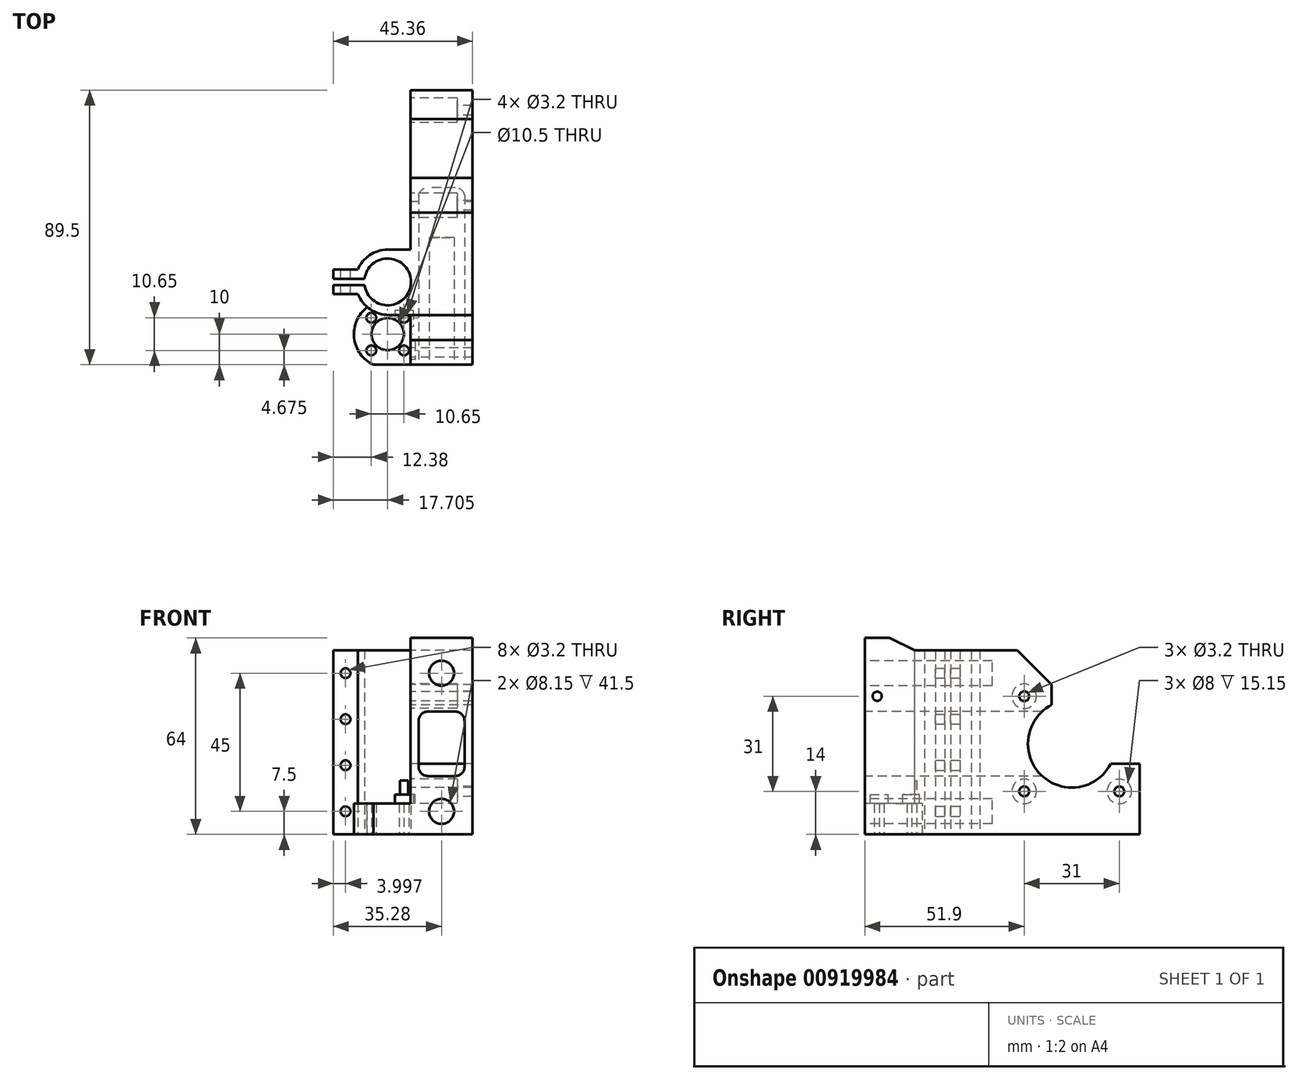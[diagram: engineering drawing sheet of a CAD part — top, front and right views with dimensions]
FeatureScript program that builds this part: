
annotation { "Feature Type Name" : "Feature", "Feature Type Description" : "" }
export const myFeature = defineFeature(function(context is Context, id is Id, definition is map)
    precondition{}
    {
        {
            var Q0;
            Q0=qCreatedBy(makeId("Top.planeOp"),FACE);
            var sketch = newSketch(context, id + "F0", { "sketchPlane" : qUnion([Q0])});
            skLineSegment(sketch, "E0.bottom", {"start": v(10.08, -44.75) * mm, "end": v(-10.07, -44.75) * mm});
            skLineSegment(sketch, "E0.top", {"start": v(10.08, 44.75) * mm, "end": v(-10.07, 44.75) * mm});
            skLineSegment(sketch, "E0.left", {"start": v(10.08, -44.75) * mm, "end": v(10.08, 44.75) * mm});
            skPoint(sketch, "E0.middle", {"position": v(0, 0) * mm});
            skCircle(sketch, "E1", {"center": v(-17.57, -34.75) * mm, "radius": 5 * mm});
            skArc(sketch, "E2", {"start": v(-17.46, -23.75) * mm, "mid": v(-17.58, -23.75) * mm, "end": v(-17.69, -23.75) * mm});
            skLineSegment(sketch, "E3", {"start": v(-17.69, -23.75) * mm, "end": v(-17.46, -23.75) * mm});
            skLineSegment(sketch, "E4", {"start": v(-10.07, -44.75) * mm, "end": v(-22.16, -44.75) * mm});
            skLineSegment(sketch, "E5.trimOffspring", {"start": v(-10.07, -7.25) * mm, "end": v(-10.07, 44.75) * mm});
            skCircle(sketch, "E6", {"center": v(-12.25, -40.08) * mm, "radius": 1.6 * mm});
            skCircle(sketch, "E7", {"center": v(-12.25, -29.43) * mm, "radius": 1.6 * mm});
            skCircle(sketch, "E8", {"center": v(-22.9, -29.43) * mm, "radius": 1.6 * mm});
            skCircle(sketch, "E9", {"center": v(-22.9, -40.08) * mm, "radius": 1.6 * mm});
            skPoint(sketch, "E10", {"position": v(-17.57, -17.75) * mm});
            skArc(sketch, "E11", {"start": v(-25, -18.75) * mm, "mid": v(-10.07, -17.75) * mm, "end": v(-25, -16.75) * mm});
            skArc(sketch, "E12", {"start": v(-17.5, -7.25) * mm, "mid": v(-23.38, -9) * mm, "end": v(-27.28, -13.75) * mm});
            skLineSegment(sketch, "E13", {"start": v(-17.66, -7.25) * mm, "end": v(-10.07, -7.25) * mm});
            skArc(sketch, "E14.trimOffspring", {"start": v(-24.15, -25.93) * mm, "mid": v(-28.51, -35.91) * mm, "end": v(-22.16, -44.75) * mm});
            skLineSegment(sketch, "E15.bottom", {"start": v(-27.28, -13.75) * mm, "end": v(-34.18, -13.75) * mm});
            skLineSegment(sketch, "E15.top", {"start": v(-27.28, -21.75) * mm, "end": v(-34.18, -21.75) * mm});
            skLineSegment(sketch, "E15.right", {"start": v(-34.18, -13.75) * mm, "end": v(-34.18, -16.75) * mm});
            skPoint(sketch, "E15.middle", {"position": v(-26.68, -17.75) * mm});
            skLineSegment(sketch, "E16.bottom", {"start": v(-25, -16.75) * mm, "end": v(-34.18, -16.75) * mm});
            skLineSegment(sketch, "E16.top", {"start": v(-25, -18.75) * mm, "end": v(-34.18, -18.75) * mm});
            skLineSegment(sketch, "E17.trimOffspring", {"start": v(-34.18, -18.75) * mm, "end": v(-34.18, -21.75) * mm});
            skArc(sketch, "E18.trimOffspring", {"start": v(-27.28, -21.75) * mm, "mid": v(-25.98, -24.04) * mm, "end": v(-24.15, -25.93) * mm});
            skLineSegment(sketch, "E19", {"start": v(-10.07, -44.75) * mm, "end": v(-10.07, -25.89) * mm});
            skLineSegment(sketch, "E20", {"start": v(-24.15, -25.93) * mm, "end": v(-10.07, -25.89) * mm});
            skSolve(sketch);
        }
        {
            var Q0;
            Q0=makeQuery(id+"F0.imprint","IMPRINT",FACE,{"disambiguationData":[TD([[makeQuery(id+"F0.imprint","IMPRINT",EDGE,{"derivedFrom":sQuery(id+"F0.wireOp",EDGE,"E1")}),-1.0]])]});
            var Q1;
            Q1=makeQuery(id+"F0.imprint","IMPRINT",FACE,{"disambiguationData":[TD([[makeQuery(id+"F0.imprint","IMPRINT",EDGE,{"derivedFrom":sQuery(id+"F0.wireOp",EDGE,"E0.bottom")}),-1.0]])]});
            extrude(context, id + "F1", {"entities" : qUnion([Q0, Q1]), "depth" : 10 * mm, "offsetDistance" : 25 * mm});
        }
        {
            var Q0;
            Q0=makeQuery(id+"F1.opExtrude","CAP_FACE",FACE,{"disambiguationData":[OSD([sQuery(id+"F0.wireOp",EDGE,"E0.bottom"),sQuery(id+"F0.wireOp",EDGE,"E0.top"),sQuery(id+"F0.wireOp",EDGE,"E0.left"),sQuery(id+"F0.wireOp",EDGE,"E1"),sQuery(id+"F0.wireOp",EDGE,"E4"),sQuery(id+"F0.wireOp",EDGE,"E5.trimOffspring"),sQuery(id+"F0.wireOp",EDGE,"E6"),sQuery(id+"F0.wireOp",EDGE,"E7"),sQuery(id+"F0.wireOp",EDGE,"E8"),sQuery(id+"F0.wireOp",EDGE,"E9"),sQuery(id+"F0.wireOp",EDGE,"E11"),sQuery(id+"F0.wireOp",EDGE,"E12"),sQuery(id+"F0.wireOp",EDGE,"E13"),sQuery(id+"F0.wireOp",EDGE,"E14.trimOffspring"),sQuery(id+"F0.wireOp",EDGE,"E15.bottom"),sQuery(id+"F0.wireOp",EDGE,"E15.top"),sQuery(id+"F0.wireOp",EDGE,"E15.right"),sQuery(id+"F0.wireOp",EDGE,"E16.bottom"),sQuery(id+"F0.wireOp",EDGE,"E16.top"),sQuery(id+"F0.wireOp",EDGE,"E17.trimOffspring"),sQuery(id+"F0.wireOp",EDGE,"E18.trimOffspring")])],"isStart":false});
            var sketch = newSketch(context, id + "F2", { "sketchPlane" : qUnion([Q0])});
            skLineSegment(sketch, "E21", {"start": v(-24.15, -25.93) * mm, "end": v(-10.07, -25.93) * mm});
            skLineSegment(sketch, "E22", {"start": v(-10.07, -25.93) * mm, "end": v(-10.07, -44.75) * mm});
            skSolve(sketch);
        }
        {
            var Q0;
            Q0=makeQuery(id+"F2.imprint","IMPRINT",FACE,{"disambiguationData":[TD([[makeQuery(id+"F2.imprint","IMPRINT",EDGE,{"derivedFrom":sQuery(id+"F2.wireOp",EDGE,"E21")}),1.0]])]});
            extrude(context, id + "F3", {"entities" : qUnion([Q0]), "operationType" : NewBodyOperationType.ADD, "depth" : 50 * mm, "offsetDistance" : 25 * mm});
        }
        {
            var Q0;
            Q0=makeQuery(id+"F3.opExtrude","CAP_FACE",FACE,{"disambiguationData":[OSD([sQuery(id+"F0.wireOp",EDGE,"E0.bottom"),sQuery(id+"F0.wireOp",EDGE,"E0.top"),sQuery(id+"F0.wireOp",EDGE,"E0.left"),sQuery(id+"F0.wireOp",EDGE,"E4"),sQuery(id+"F0.wireOp",EDGE,"E5.trimOffspring"),sQuery(id+"F0.wireOp",EDGE,"E11"),sQuery(id+"F0.wireOp",EDGE,"E12"),sQuery(id+"F0.wireOp",EDGE,"E13"),sQuery(id+"F0.wireOp",EDGE,"E15.bottom"),sQuery(id+"F0.wireOp",EDGE,"E15.top"),sQuery(id+"F0.wireOp",EDGE,"E15.right"),sQuery(id+"F0.wireOp",EDGE,"E16.bottom"),sQuery(id+"F0.wireOp",EDGE,"E16.top"),sQuery(id+"F0.wireOp",EDGE,"E17.trimOffspring"),sQuery(id+"F0.wireOp",EDGE,"E18.trimOffspring"),sQuery(id+"F2.wireOp",EDGE,"E21"),sQuery(id+"F2.wireOp",EDGE,"E22")])],"isStart":false});
            var sketch = newSketch(context, id + "F4", { "sketchPlane" : qUnion([Q0])});
            skArc(sketch, "E23", {"start": v(-27.28, -21.75) * mm, "mid": v(-23.23, -26.7) * mm, "end": v(-17.11, -28.53) * mm});
            skPoint(sketch, "E24.startSnap0", {"position": v(-17.11, -25.93) * mm});
            skLineSegment(sketch, "E25", {"start": v(-17.11, -28.53) * mm, "end": v(-10.07, -28.53) * mm});
            skSolve(sketch);
        }
        {
            var Q0;
            Q0=makeQuery(id+"F4.imprint","IMPRINT",FACE,{"disambiguationData":[TD([[makeQuery(id+"F4.imprint","IMPRINT",EDGE,{"derivedFrom":sQuery(id+"F4.wireOp",EDGE,"E23")}),1.0]])]});
            extrude(context, id + "F5", {"entities" : qUnion([Q0]), "operationType" : NewBodyOperationType.ADD, "oppositeDirection" : true, "depth" : 50 * mm, "offsetDistance" : 25 * mm});
        }
        {
            var Q0;
            Q0=makeQuery(id+"F5.opExtrude","SWEPT_FACE",FACE,{"disambiguationData":[OSD([sQuery(id+"F4.wireOp",EDGE,"E25")])]});
            var sketch = newSketch(context, id + "F6", { "sketchPlane" : qUnion([Q0])});
            skLineSegment(sketch, "E26.bottom", {"start": v(-9.25, 10) * mm, "end": v(-15.25, 10) * mm});
            skLineSegment(sketch, "E26.top", {"start": v(-9.25, 13) * mm, "end": v(-15.25, 13) * mm});
            skLineSegment(sketch, "E26.left", {"start": v(-9.25, 10) * mm, "end": v(-9.25, 13) * mm});
            skLineSegment(sketch, "E26.right", {"start": v(-15.25, 10) * mm, "end": v(-15.25, 13) * mm});
            skPoint(sketch, "E26.middle", {"position": v(-12.25, 11.5) * mm});
            skSolve(sketch);
        }
        {
            var Q0;
            Q0 = qSketchRegion(id + "F6", true);
            extrude(context, id + "F7", {"entities" : qUnion([Q0]), "operationType" : NewBodyOperationType.REMOVE, "oppositeDirection" : true, "depth" : 1.5 * mm, "offsetDistance" : 25 * mm});
        }
        {
            var Q0;
            Q0=makeQuery(id+"F7.boolean.opBoolean","MERGE",FACE,{"derivedFrom":[makeQuery(id+"F1.opExtrude","CAP_FACE",FACE,{"disambiguationData":[OSD([sQuery(id+"F0.wireOp",EDGE,"E0.bottom"),sQuery(id+"F0.wireOp",EDGE,"E0.top"),sQuery(id+"F0.wireOp",EDGE,"E0.left"),sQuery(id+"F0.wireOp",EDGE,"E1"),sQuery(id+"F0.wireOp",EDGE,"E4"),sQuery(id+"F0.wireOp",EDGE,"E5.trimOffspring"),sQuery(id+"F0.wireOp",EDGE,"E6"),sQuery(id+"F0.wireOp",EDGE,"E7"),sQuery(id+"F0.wireOp",EDGE,"E8"),sQuery(id+"F0.wireOp",EDGE,"E9"),sQuery(id+"F0.wireOp",EDGE,"E11"),sQuery(id+"F0.wireOp",EDGE,"E12"),sQuery(id+"F0.wireOp",EDGE,"E13"),sQuery(id+"F0.wireOp",EDGE,"E14.trimOffspring"),sQuery(id+"F0.wireOp",EDGE,"E15.bottom"),sQuery(id+"F0.wireOp",EDGE,"E15.top"),sQuery(id+"F0.wireOp",EDGE,"E15.right"),sQuery(id+"F0.wireOp",EDGE,"E16.bottom"),sQuery(id+"F0.wireOp",EDGE,"E16.top"),sQuery(id+"F0.wireOp",EDGE,"E17.trimOffspring"),sQuery(id+"F0.wireOp",EDGE,"E18.trimOffspring")])],"isStart":false})],"fromTools":[makeQuery(id+"F7.opExtrude","SWEPT_FACE",FACE,{"disambiguationData":[OSD([sQuery(id+"F6.wireOp",EDGE,"E26.bottom")])]})]});
            var sketch = newSketch(context, id + "F8", { "sketchPlane" : qUnion([Q0])});
            skCircle(sketch, "E27", {"center": v(-12.25, -29.43) * mm, "radius": 1.6 * mm});
            skCircle(sketch, "E28", {"center": v(-12.25, -40.08) * mm, "radius": 1.6 * mm});
            skSolve(sketch);
        }
        {
            var Q0;
            Q0=makeQuery(id+"F3.opExtrude","SWEPT_FACE",FACE,{"disambiguationData":[OSD([sQuery(id+"F2.wireOp",EDGE,"E22")])]});
            var sketch = newSketch(context, id + "F9", { "sketchPlane" : qUnion([Q0])});
            skLineSegment(sketch, "E29.bottom", {"start": v(32.43, 10) * mm, "end": v(26.43, 10) * mm});
            skLineSegment(sketch, "E29.top", {"start": v(32.43, 13) * mm, "end": v(26.43, 13) * mm});
            skLineSegment(sketch, "E29.left", {"start": v(32.43, 10) * mm, "end": v(32.43, 13) * mm});
            skLineSegment(sketch, "E29.right", {"start": v(26.43, 10) * mm, "end": v(26.43, 13) * mm});
            skPoint(sketch, "E29.middle", {"position": v(29.43, 11.5) * mm});
            skLineSegment(sketch, "E30.bottom", {"start": v(43.03, 10) * mm, "end": v(37.12, 10) * mm});
            skLineSegment(sketch, "E30.top", {"start": v(43.03, 13) * mm, "end": v(37.12, 13) * mm});
            skLineSegment(sketch, "E30.left", {"start": v(43.03, 10) * mm, "end": v(43.03, 13) * mm});
            skLineSegment(sketch, "E30.right", {"start": v(37.12, 10) * mm, "end": v(37.12, 13) * mm});
            skPoint(sketch, "E30.middle", {"position": v(40.08, 11.5) * mm});
            skSolve(sketch);
        }
        {
            var Q0;
            {var subQ6=sQuery(id+"F9.wireOp",EDGE,"E29.left");Q0=makeQuery(id+"F9.imprint","IMPRINT",FACE,{"disambiguationData":[TD([[makeQuery(id+"F9.imprint","IMPRINT",EDGE,{"derivedFrom":subQ6}),1.0]])]});}
            var Q1;
            Q1=makeQuery(id+"F9.imprint","IMPRINT",FACE,{"disambiguationData":[TD([[makeQuery(id+"F9.imprint","IMPRINT",EDGE,{"derivedFrom":sQuery(id+"F9.wireOp",EDGE,"E30.bottom")}),1.0]])]});
            extrude(context, id + "F10", {"entities" : qUnion([Q0, Q1]), "operationType" : NewBodyOperationType.REMOVE, "oppositeDirection" : true, "depth" : 1.5 * mm, "offsetDistance" : 25 * mm});
        }
        {
            var Q0;
            Q0=makeQuery(id+"F10.boolean.opBoolean","COPY",FACE,{"derivedFrom":makeQuery(id+"F10.opExtrude","SWEPT_FACE",FACE,{"disambiguationData":[OSD([sQuery(id+"F2.wireOp",EDGE,"E22"),sQuery(id+"F4.wireOp",EDGE,"E25")])]})});
            extrude(context, id + "F11", {"entities" : qUnion([Q0]), "operationType" : NewBodyOperationType.ADD, "depth" : 3.97 * mm, "offsetDistance" : 25 * mm});
        }
        {
            var Q0;
            {var subQ0=sQuery(id+"F0.wireOp",EDGE,"E15.bottom");Q0=makeQuery(id+"F3.boolean.opBoolean","MERGE",FACE,{"derivedFrom":[makeQuery(id+"F1.opExtrude","SWEPT_FACE",FACE,{"disambiguationData":[OSD([subQ0])]}),makeQuery(id+"F3.opExtrude","SWEPT_FACE",FACE,{"disambiguationData":[OSD([subQ0])]})]});}
            var sketch = newSketch(context, id + "F12", { "sketchPlane" : qUnion([Q0])});
            skCircle(sketch, "E31", {"center": v(31.28, 52.5) * mm, "radius": 1.6 * mm});
            skCircle(sketch, "E32", {"center": v(31.28, 37.5) * mm, "radius": 1.6 * mm});
            skCircle(sketch, "E33", {"center": v(31.28, 22.5) * mm, "radius": 1.6 * mm});
            skCircle(sketch, "E34", {"center": v(31.28, 7.5) * mm, "radius": 1.6 * mm});
            skSolve(sketch);
        }
        {
            var Q0;
            Q0=makeQuery(id+"F12.imprint","IMPRINT",FACE,{"disambiguationData":[TD([[makeQuery(id+"F12.imprint","IMPRINT",EDGE,{"derivedFrom":sQuery(id+"F12.wireOp",EDGE,"E31")}),1.0]])]});
            var Q1;
            Q1=makeQuery(id+"F12.imprint","IMPRINT",FACE,{"disambiguationData":[TD([[makeQuery(id+"F12.imprint","IMPRINT",EDGE,{"derivedFrom":sQuery(id+"F12.wireOp",EDGE,"E32")}),1.0]])]});
            var Q2;
            Q2=makeQuery(id+"F12.imprint","IMPRINT",FACE,{"disambiguationData":[TD([[makeQuery(id+"F12.imprint","IMPRINT",EDGE,{"derivedFrom":sQuery(id+"F12.wireOp",EDGE,"E33")}),1.0]])]});
            var Q3;
            Q3=makeQuery(id+"F12.imprint","IMPRINT",FACE,{"disambiguationData":[TD([[makeQuery(id+"F12.imprint","IMPRINT",EDGE,{"derivedFrom":sQuery(id+"F12.wireOp",EDGE,"E34")}),1.0]])]});
            extrude(context, id + "F13", {"entities" : qUnion([Q0, Q1, Q2, Q3]), "operationType" : NewBodyOperationType.REMOVE, "oppositeDirection" : true, "depth" : 25 * mm, "offsetDistance" : 25 * mm});
        }
        {
            var Q0;
            {var subQ0=sQuery(id+"F0.wireOp",EDGE,"E15.right");Q0=makeQuery(id+"F3.boolean.opBoolean","MERGE",FACE,{"derivedFrom":[makeQuery(id+"F1.opExtrude","SWEPT_FACE",FACE,{"disambiguationData":[OSD([subQ0])]}),makeQuery(id+"F3.opExtrude","SWEPT_FACE",FACE,{"disambiguationData":[OSD([subQ0])]})]});}
            var Q1;
            {var subQ0=sQuery(id+"F0.wireOp",EDGE,"E17.trimOffspring");Q1=makeQuery(id+"F3.boolean.opBoolean","MERGE",FACE,{"derivedFrom":[makeQuery(id+"F1.opExtrude","SWEPT_FACE",FACE,{"disambiguationData":[OSD([subQ0])]}),makeQuery(id+"F3.opExtrude","SWEPT_FACE",FACE,{"disambiguationData":[OSD([subQ0])]})]});}
            extrude(context, id + "F14", {"entities" : qUnion([Q0, Q1]), "operationType" : NewBodyOperationType.ADD, "depth" : 1.1 * mm, "offsetDistance" : 25 * mm});
        }
        {
            var Q0;
            {var subQ0=sQuery(id+"F0.wireOp",EDGE,"E14.trimOffspring");var subQ1=sQuery(id+"F0.wireOp",EDGE,"E18.trimOffspring");var subQ3=sQuery(id+"F4.wireOp",EDGE,"E23");Q0=makeQuery(id+"F5.boolean.opBoolean","SPLIT",FACE,{"disambiguationData":[TD([makeQuery(id+"F1.opExtrude","SWEPT_FACE",FACE,{"disambiguationData":[OSD([subQ0])]})])],"derivedFrom":makeQuery(id+"F5.opExtrude","CAP_FACE",FACE,{"disambiguationData":[OSD([subQ1,sQuery(id+"F2.wireOp",EDGE,"E21"),sQuery(id+"F2.wireOp",EDGE,"E22"),subQ3,sQuery(id+"F4.wireOp",EDGE,"E25")])],"isStart":false})});}
            extrude(context, id + "F15", {"entities" : qUnion([Q0]), "operationType" : NewBodyOperationType.ADD, "depth" : 10 * mm, "offsetDistance" : 25 * mm});
        }
        {
            var Q0;
            {var subQ0=sQuery(id+"F0.wireOp",EDGE,"E5.trimOffspring");Q0=makeQuery(id+"F3.boolean.opBoolean","MERGE",FACE,{"derivedFrom":[makeQuery(id+"F1.opExtrude","SWEPT_FACE",FACE,{"disambiguationData":[OSD([subQ0])]}),makeQuery(id+"F3.opExtrude","SWEPT_FACE",FACE,{"disambiguationData":[OSD([subQ0])]})]});}
            var sketch = newSketch(context, id + "F16", { "sketchPlane" : qUnion([Q0])});
            skCircle(sketch, "E35", {"center": v(-38.15, 14) * mm, "radius": 1.6 * mm});
            skCircle(sketch, "E36", {"center": v(-7.15, 45) * mm, "radius": 1.6 * mm});
            skCircle(sketch, "E37", {"center": v(-7.15, 14) * mm, "radius": 1.6 * mm});
            skCircle(sketch, "E38", {"center": v(-7.15, 45) * mm, "radius": 4 * mm});
            skCircle(sketch, "E39", {"center": v(-7.15, 14) * mm, "radius": 4 * mm});
            skCircle(sketch, "E40", {"center": v(-38.15, 14) * mm, "radius": 4 * mm});
            skSolve(sketch);
        }
        {
            var Q0;
            Q0=makeQuery(id+"F16.imprint","IMPRINT",FACE,{"disambiguationData":[TD([[makeQuery(id+"F16.imprint","IMPRINT",EDGE,{"derivedFrom":sQuery(id+"F16.wireOp",EDGE,"E36")}),1.0]])]});
            var Q1;
            Q1=makeQuery(id+"F16.imprint","IMPRINT",FACE,{"disambiguationData":[TD([[makeQuery(id+"F16.imprint","IMPRINT",EDGE,{"derivedFrom":sQuery(id+"F16.wireOp",EDGE,"E37")}),1.0]])]});
            var Q2;
            Q2=makeQuery(id+"F16.imprint","IMPRINT",FACE,{"disambiguationData":[TD([[makeQuery(id+"F16.imprint","IMPRINT",EDGE,{"derivedFrom":sQuery(id+"F16.wireOp",EDGE,"E35")}),1.0]])]});
            extrude(context, id + "F17", {"entities" : qUnion([Q0, Q1, Q2]), "operationType" : NewBodyOperationType.REMOVE, "endBound" : BoundingType.THROUGH_ALL, "oppositeDirection" : true, "depth" : 25 * mm, "offsetDistance" : 25 * mm});
        }
        {
            var Q0;
            Q0=makeQuery(id+"F16.imprint","IMPRINT",FACE,{"disambiguationData":[TD([[makeQuery(id+"F16.imprint","IMPRINT",EDGE,{"derivedFrom":sQuery(id+"F16.wireOp",EDGE,"E36")}),-1.0]])]});
            var Q1;
            Q1=makeQuery(id+"F16.imprint","IMPRINT",FACE,{"disambiguationData":[TD([[makeQuery(id+"F16.imprint","IMPRINT",EDGE,{"derivedFrom":sQuery(id+"F16.wireOp",EDGE,"E37")}),-1.0]])]});
            var Q2;
            Q2=makeQuery(id+"F16.imprint","IMPRINT",FACE,{"disambiguationData":[TD([[makeQuery(id+"F16.imprint","IMPRINT",EDGE,{"derivedFrom":sQuery(id+"F16.wireOp",EDGE,"E35")}),-1.0]])]});
            extrude(context, id + "F18", {"entities" : qUnion([Q0, Q1, Q2]), "operationType" : NewBodyOperationType.REMOVE, "oppositeDirection" : true, "depth" : 17.15 * mm, "offsetDistance" : 25 * mm});
        }
        {
            var Q0;
            {var subQ0=sQuery(id+"F0.wireOp",EDGE,"E5.trimOffspring");Q0=makeQuery(id+"F3.boolean.opBoolean","MERGE",FACE,{"derivedFrom":[makeQuery(id+"F1.opExtrude","SWEPT_FACE",FACE,{"disambiguationData":[OSD([subQ0])]}),makeQuery(id+"F3.opExtrude","SWEPT_FACE",FACE,{"disambiguationData":[OSD([subQ0])]})]});}
            var sketch = newSketch(context, id + "F19", { "sketchPlane" : qUnion([Q0])});
            skCircle(sketch, "E41", {"center": v(-22.65, 29.5) * mm, "radius": 14.25 * mm});
            skCircle(sketch, "E42", {"center": v(-7.15, 45) * mm, "radius": 0.81 * mm});
            skCircle(sketch, "E43", {"center": v(-7.15, 14) * mm, "radius": 1.4 * mm});
            skCircle(sketch, "E44", {"center": v(-38.15, 14) * mm, "radius": 0.92 * mm});
            skSolve(sketch);
        }
        {
            var Q0;
            Q0=makeQuery(id+"F19.imprint","IMPRINT",FACE,{"disambiguationData":[TD([[makeQuery(id+"F19.imprint","IMPRINT",EDGE,{"derivedFrom":sQuery(id+"F19.wireOp",EDGE,"E41")}),1.0]])]});
            extrude(context, id + "F20", {"entities" : qUnion([Q0]), "operationType" : NewBodyOperationType.REMOVE, "endBound" : BoundingType.THROUGH_ALL, "oppositeDirection" : true, "depth" : 25 * mm, "offsetDistance" : 25 * mm});
        }
        {
            var Q0;
            {var subQ0=sQuery(id+"F0.wireOp",EDGE,"E4");var subQ1=sQuery(id+"F0.wireOp",EDGE,"E0.bottom");Q0=makeQuery(id+"F3.boolean.opBoolean","MERGE",FACE,{"derivedFrom":[makeQuery(id+"F1.opExtrude","SWEPT_FACE",FACE,{"disambiguationData":[OSD([subQ1,subQ0])]}),makeQuery(id+"F3.opExtrude","SWEPT_FACE",FACE,{"disambiguationData":[OSD([subQ1,subQ0])]})]});}
            var sketch = newSketch(context, id + "F21", { "sketchPlane" : qUnion([Q0])});
            skLineSegment(sketch, "E45.bottom", {"start": v(7.48, 19) * mm, "end": v(-7.47, 19) * mm});
            skLineSegment(sketch, "E45.top", {"start": v(7.48, 40) * mm, "end": v(-7.47, 40) * mm});
            skLineSegment(sketch, "E45.left", {"start": v(7.48, 19) * mm, "end": v(7.47, 40) * mm});
            skLineSegment(sketch, "E45.right", {"start": v(-7.47, 19) * mm, "end": v(-7.47, 40) * mm});
            skPoint(sketch, "E45.middle", {"position": v(0, 29.5) * mm});
            skSolve(sketch);
        }
        {
            var Q0;
            Q0 = qSketchRegion(id + "F21", true);
            extrude(context, id + "F22", {"entities" : qUnion([Q0]), "operationType" : NewBodyOperationType.REMOVE, "oppositeDirection" : true, "depth" : 62.2 * mm, "offsetDistance" : 25 * mm});
        }
        {
            var Q0;
            {var subQ0=sQuery(id+"F0.wireOp",EDGE,"E5.trimOffspring");Q0=makeQuery(id+"F3.boolean.opBoolean","MERGE",FACE,{"derivedFrom":[makeQuery(id+"F1.opExtrude","SWEPT_FACE",FACE,{"disambiguationData":[OSD([subQ0])]}),makeQuery(id+"F3.opExtrude","SWEPT_FACE",FACE,{"disambiguationData":[OSD([subQ0])]})]});}
            var sketch = newSketch(context, id + "F23", { "sketchPlane" : qUnion([Q0])});
            skLineSegment(sketch, "E46", {"start": v(-35.33, 23) * mm, "end": v(-44.75, 23) * mm});
            skLineSegment(sketch, "E47", {"start": v(-16.15, 42.18) * mm, "end": v(-16.15, 48.73) * mm});
            skLineSegment(sketch, "E48", {"start": v(-16.15, 48.73) * mm, "end": v(-4.88, 60) * mm});
            skSolve(sketch);
        }
        {
            var Q0;
            Q0 = qSketchRegion(id + "F23", true);
            var Q1;
            {var subQ7=sQuery(id+"F23.wireOp",EDGE,"E46");Q1=makeQuery(id+"F23.imprint","IMPRINT",FACE,{"disambiguationData":[TD([[makeQuery(id+"F23.imprint","IMPRINT",EDGE,{"derivedFrom":subQ7}),-1.0]])]});}
            extrude(context, id + "F24", {"entities" : qUnion([Q0, Q1]), "operationType" : NewBodyOperationType.REMOVE, "endBound" : BoundingType.THROUGH_ALL, "oppositeDirection" : true, "depth" : 25 * mm, "offsetDistance" : 25 * mm});
        }
        {
            var Q0;
            Q0=makeQuery(id+"F3.opExtrude","SWEPT_FACE",FACE,{"disambiguationData":[OSD([sQuery(id+"F2.wireOp",EDGE,"E22")])]});
            var sketch = newSketch(context, id + "F25", { "sketchPlane" : qUnion([Q0])});
            skCircle(sketch, "E49", {"center": v(40.75, 56) * mm, "radius": 1.5 * mm});
            skCircle(sketch, "E50", {"center": v(40.75, 45) * mm, "radius": 1.5 * mm});
            skSolve(sketch);
        }
        {
            var Q0;
            Q0=makeQuery(id+"F25.imprint","IMPRINT",FACE,{"disambiguationData":[TD([[makeQuery(id+"F25.imprint","IMPRINT",EDGE,{"derivedFrom":sQuery(id+"F25.wireOp",EDGE,"E49")}),1.0]])]});
            extrude(context, id + "F26", {"entities" : qUnion([Q0]), "operationType" : NewBodyOperationType.REMOVE, "oppositeDirection" : true, "depth" : 6 * mm, "offsetDistance" : 25 * mm});
        }
        {
            var Q0;
            {var subQ0=sQuery(id+"F0.wireOp",EDGE,"E4");var subQ1=sQuery(id+"F0.wireOp",EDGE,"E0.bottom");Q0=makeQuery(id+"F3.boolean.opBoolean","MERGE",FACE,{"derivedFrom":[makeQuery(id+"F1.opExtrude","SWEPT_FACE",FACE,{"disambiguationData":[OSD([subQ1,subQ0])]}),makeQuery(id+"F3.opExtrude","SWEPT_FACE",FACE,{"disambiguationData":[OSD([subQ1,subQ0])]})]});}
            var sketch = newSketch(context, id + "F27", { "sketchPlane" : qUnion([Q0])});
            skCircle(sketch, "E51", {"center": v(0, 52.5) * mm, "radius": 4 * mm});
            skCircle(sketch, "E52", {"center": v(0, 7.5) * mm, "radius": 4 * mm});
            skSolve(sketch);
        }
        {
            var Q0;
            Q0=makeQuery(id+"F27.imprint","IMPRINT",FACE,{"disambiguationData":[TD([[makeQuery(id+"F27.imprint","IMPRINT",EDGE,{"derivedFrom":sQuery(id+"F27.wireOp",EDGE,"E51")}),1.0]])]});
            var Q1;
            Q1=makeQuery(id+"F27.imprint","IMPRINT",FACE,{"disambiguationData":[TD([[makeQuery(id+"F27.imprint","IMPRINT",EDGE,{"derivedFrom":sQuery(id+"F27.wireOp",EDGE,"E52")}),1.0]])]});
            extrude(context, id + "F28", {"entities" : qUnion([Q0, Q1]), "operationType" : NewBodyOperationType.REMOVE, "oppositeDirection" : true, "depth" : 41.5 * mm, "offsetDistance" : 25 * mm});
        }
        {
            var Q0;
            Q0=makeQuery(id+"F25.imprint","IMPRINT",FACE,{"disambiguationData":[TD([[makeQuery(id+"F25.imprint","IMPRINT",EDGE,{"derivedFrom":sQuery(id+"F25.wireOp",EDGE,"E50")}),1.0]])]});
            var Q1;
            Q1=makeQuery(id+"F25.imprint","IMPRINT",FACE,{"disambiguationData":[TD([[makeQuery(id+"F25.imprint","IMPRINT",EDGE,{"derivedFrom":sQuery(id+"F25.wireOp",EDGE,"E49")}),1.0]])]});
            extrude(context, id + "F29", {"entities" : qUnion([Q0, Q1]), "operationType" : NewBodyOperationType.REMOVE, "endBound" : BoundingType.THROUGH_ALL, "oppositeDirection" : true, "depth" : 25 * mm, "offsetDistance" : 25 * mm});
        }
        {
            var Q0;
            {var subQ0=sQuery(id+"F0.wireOp",EDGE,"E0.left");Q0=makeQuery(id+"F3.boolean.opBoolean","MERGE",FACE,{"derivedFrom":[makeQuery(id+"F1.opExtrude","SWEPT_FACE",FACE,{"disambiguationData":[OSD([subQ0])]}),makeQuery(id+"F3.opExtrude","SWEPT_FACE",FACE,{"disambiguationData":[OSD([subQ0])]})]});}
            var sketch = newSketch(context, id + "F30", { "sketchPlane" : qUnion([Q0])});
            skCircle(sketch, "E53", {"center": v(-40.75, 56) * mm, "radius": 1.5 * mm});
            skSolve(sketch);
        }
        {
            var Q0;
            Q0=makeQuery(id+"F30.imprint","IMPRINT",FACE,{"disambiguationData":[TD([[makeQuery(id+"F30.imprint","IMPRINT",EDGE,{"derivedFrom":sQuery(id+"F30.wireOp",EDGE,"E53")}),-1.0]])]});
            extrude(context, id + "F31", {"entities" : qUnion([Q0]), "operationType" : NewBodyOperationType.ADD, "oppositeDirection" : true, "depth" : 14.3 * mm, "offsetDistance" : 25 * mm});
        }
        {
            var Q0;
            Q0=makeQuery(id+"F28.boolean.opBoolean","COPY",FACE,{"derivedFrom":makeQuery(id+"F28.opExtrude","CAP_FACE",FACE,{"disambiguationData":[OSD([sQuery(id+"F27.wireOp",EDGE,"E51")])],"isStart":false})});
            extrude(context, id + "F32", {"entities" : qUnion([Q0]), "operationType" : NewBodyOperationType.REMOVE, "depth" : 44.5 * mm, "offsetDistance" : 25 * mm});
        }
        {
            var Q0;
            Q0=makeQuery(id+"F18.boolean.opBoolean","COPY",FACE,{"derivedFrom":makeQuery(id+"F18.opExtrude","CAP_FACE",FACE,{"disambiguationData":[OSD([sQuery(id+"F16.wireOp",EDGE,"E36"),sQuery(id+"F16.wireOp",EDGE,"E38")])],"isStart":false})});
            var Q1;
            Q1=makeQuery(id+"F18.boolean.opBoolean","COPY",FACE,{"derivedFrom":makeQuery(id+"F18.opExtrude","CAP_FACE",FACE,{"disambiguationData":[OSD([sQuery(id+"F16.wireOp",EDGE,"E37"),sQuery(id+"F16.wireOp",EDGE,"E39")])],"isStart":false})});
            var Q2;
            Q2=makeQuery(id+"F18.boolean.opBoolean","COPY",FACE,{"derivedFrom":makeQuery(id+"F18.opExtrude","CAP_FACE",FACE,{"disambiguationData":[OSD([sQuery(id+"F16.wireOp",EDGE,"E35"),sQuery(id+"F16.wireOp",EDGE,"E40")])],"isStart":false})});
            extrude(context, id + "F33", {"entities" : qUnion([Q0, Q1, Q2]), "operationType" : NewBodyOperationType.ADD, "depth" : 2 * mm, "offsetDistance" : 25 * mm});
        }
        {
            var Q0;
            Q0=makeQuery(id+"F22.boolean.opBoolean","COPY",EDGE,{"derivedFrom":makeQuery(id+"F22.opExtrude","SWEPT_EDGE",EDGE,{"disambiguationData":[OSD([sQuery(id+"F21.wireOp",EDGE,"E45.bottom"),sQuery(id+"F21.wireOp",EDGE,"E45.right")])]})});
            var Q1;
            Q1=makeQuery(id+"F22.boolean.opBoolean","COPY",EDGE,{"derivedFrom":makeQuery(id+"F22.opExtrude","SWEPT_EDGE",EDGE,{"disambiguationData":[OSD([sQuery(id+"F21.wireOp",EDGE,"E45.bottom"),sQuery(id+"F21.wireOp",EDGE,"E45.left")])]})});
            var Q2;
            Q2=makeQuery(id+"F22.boolean.opBoolean","COPY",EDGE,{"derivedFrom":makeQuery(id+"F22.opExtrude","SWEPT_EDGE",EDGE,{"disambiguationData":[OSD([sQuery(id+"F21.wireOp",EDGE,"E45.top"),sQuery(id+"F21.wireOp",EDGE,"E45.right")])]})});
            var Q3;
            Q3=makeQuery(id+"F22.boolean.opBoolean","COPY",EDGE,{"derivedFrom":makeQuery(id+"F22.opExtrude","SWEPT_EDGE",EDGE,{"disambiguationData":[OSD([sQuery(id+"F21.wireOp",EDGE,"E45.top"),sQuery(id+"F21.wireOp",EDGE,"E45.left")])]})});
            fillet(context, id + "F34", {"entities" : qUnion([Q0, Q1, Q2, Q3]), "radius" : 3 * mm, "tangentPropagation" : true, "allowEdgeOverflow" : false});
        }
        {
            var Q0;
            Q0=makeQuery(id+"F8.imprint","IMPRINT",FACE,{"disambiguationData":[TD([[makeQuery(id+"F8.imprint","IMPRINT",EDGE,{"derivedFrom":sQuery(id+"F8.wireOp",EDGE,"E27")}),1.0]])]});
            extrude(context, id + "F35", {"entities" : qUnion([Q0]), "operationType" : NewBodyOperationType.REMOVE, "depth" : 7.5 * mm, "offsetDistance" : 25 * mm});
        }
        {
            var Q0;
            {var subQ0=sQuery(id+"F0.wireOp",EDGE,"E18.trimOffspring");var subQ1=sQuery(id+"F0.wireOp",EDGE,"E17.trimOffspring");var subQ2=sQuery(id+"F0.wireOp",EDGE,"E15.right");Q0=makeQuery(id+"F15.boolean.opBoolean","MERGE",FACE,{"derivedFrom":[makeQuery(id+"F14.boolean.opBoolean","MERGE",FACE,{"derivedFrom":[makeQuery(id+"F1.opExtrude","CAP_FACE",FACE,{"disambiguationData":[OSD([sQuery(id+"F0.wireOp",EDGE,"E0.bottom"),sQuery(id+"F0.wireOp",EDGE,"E0.top"),sQuery(id+"F0.wireOp",EDGE,"E0.left"),sQuery(id+"F0.wireOp",EDGE,"E1"),sQuery(id+"F0.wireOp",EDGE,"E4"),sQuery(id+"F0.wireOp",EDGE,"E5.trimOffspring"),sQuery(id+"F0.wireOp",EDGE,"E6"),sQuery(id+"F0.wireOp",EDGE,"E7"),sQuery(id+"F0.wireOp",EDGE,"E8"),sQuery(id+"F0.wireOp",EDGE,"E9"),sQuery(id+"F0.wireOp",EDGE,"E11"),sQuery(id+"F0.wireOp",EDGE,"E12"),sQuery(id+"F0.wireOp",EDGE,"E13"),sQuery(id+"F0.wireOp",EDGE,"E14.trimOffspring"),sQuery(id+"F0.wireOp",EDGE,"E15.bottom"),sQuery(id+"F0.wireOp",EDGE,"E15.top"),subQ2,sQuery(id+"F0.wireOp",EDGE,"E16.bottom"),sQuery(id+"F0.wireOp",EDGE,"E16.top"),subQ1,subQ0])],"isStart":true}),makeQuery(id+"F14.opExtrude","SWEPT_FACE",FACE,{"disambiguationData":[OSD([subQ2]),TDD([makeQuery(id+"F1.opExtrude","CAP_EDGE",EDGE,{"disambiguationData":[OSD([subQ2])],"isStart":true})])]}),makeQuery(id+"F14.opExtrude","SWEPT_FACE",FACE,{"disambiguationData":[OSD([subQ1]),TDD([makeQuery(id+"F1.opExtrude","CAP_EDGE",EDGE,{"disambiguationData":[OSD([subQ1])],"isStart":true})])]})]}),makeQuery(id+"F15.opExtrude","CAP_FACE",FACE,{"disambiguationData":[OSD([subQ0,sQuery(id+"F2.wireOp",EDGE,"E21"),sQuery(id+"F2.wireOp",EDGE,"E22"),sQuery(id+"F4.wireOp",EDGE,"E23"),sQuery(id+"F4.wireOp",EDGE,"E25")])],"isStart":false})]});}
            var sketch = newSketch(context, id + "F36", { "sketchPlane" : qUnion([Q0])});
            skCircle(sketch, "E54", {"center": v(-17.57, 17.75) * mm, "radius": 7.62 * mm});
            skCircle(sketch, "E55", {"center": v(-17.57, 34.75) * mm, "radius": 5.25 * mm});
            skSolve(sketch);
        }
        {
            var Q0;
            Q0 = qSketchRegion(id + "F36", true);
            extrude(context, id + "F37", {"entities" : qUnion([Q0]), "operationType" : NewBodyOperationType.REMOVE, "endBound" : BoundingType.THROUGH_ALL, "oppositeDirection" : true, "depth" : 25 * mm, "offsetDistance" : 25 * mm});
        }
        {
            var Q0;
            {var subQ0=sQuery(id+"F0.wireOp",EDGE,"E4");var subQ1=sQuery(id+"F0.wireOp",EDGE,"E0.bottom");Q0=makeQuery(id+"F3.boolean.opBoolean","MERGE",FACE,{"derivedFrom":[makeQuery(id+"F1.opExtrude","SWEPT_FACE",FACE,{"disambiguationData":[OSD([subQ1,subQ0])]}),makeQuery(id+"F3.opExtrude","SWEPT_FACE",FACE,{"disambiguationData":[OSD([subQ1,subQ0])]})]});}
            var sketch = newSketch(context, id + "F38", { "sketchPlane" : qUnion([Q0])});
            skCircle(sketch, "E56", {"center": v(0, 7.5) * mm, "radius": 4.08 * mm});
            skCircle(sketch, "E57", {"center": v(0, 52.5) * mm, "radius": 4.08 * mm});
            skSolve(sketch);
        }
        {
            var Q0;
            Q0 = qSketchRegion(id + "F38", true);
            extrude(context, id + "F39", {"entities" : qUnion([Q0]), "operationType" : NewBodyOperationType.REMOVE, "oppositeDirection" : true, "depth" : 41.5 * mm, "offsetDistance" : 25 * mm});
        }
        {
            var Q0;
            Q0=makeQuery(id+"F31.opExtrude","CAP_FACE",FACE,{"disambiguationData":[OSD([sQuery(id+"F30.wireOp",EDGE,"E53")])],"isStart":false});
            extrude(context, id + "F40", {"entities" : qUnion([Q0]), "operationType" : NewBodyOperationType.ADD, "depth" : 5.85 * mm, "offsetDistance" : 25 * mm});
        }
        {
            var Q0;
            Q0=makeQuery(id+"F40.boolean.opBoolean","MERGE",FACE,{"derivedFrom":[makeQuery(id+"F3.opExtrude","SWEPT_FACE",FACE,{"disambiguationData":[OSD([sQuery(id+"F2.wireOp",EDGE,"E22")])]}),makeQuery(id+"F40.opExtrude","CAP_FACE",FACE,{"disambiguationData":[OSD([sQuery(id+"F30.wireOp",EDGE,"E53")])],"isStart":false})]});
            var sketch = newSketch(context, id + "F41", { "sketchPlane" : qUnion([Q0])});
            skLineSegment(sketch, "E58.top", {"start": v(44.75, 64) * mm, "end": v(36.75, 64) * mm});
            skLineSegment(sketch, "E58.left", {"start": v(44.75, 60) * mm, "end": v(44.75, 64) * mm});
            skLineSegment(sketch, "E59", {"start": v(36.75, 64) * mm, "end": v(28.53, 60) * mm});
            skSolve(sketch);
        }
        {
            var Q0;
            Q0=makeQuery(id+"F41.imprint","IMPRINT",FACE,{"disambiguationData":[TD([[makeQuery(id+"F41.imprint","IMPRINT",EDGE,{"derivedFrom":sQuery(id+"F41.wireOp",EDGE,"E58.top")}),1.0]])]});
            extrude(context, id + "F42", {"entities" : qUnion([Q0]), "operationType" : NewBodyOperationType.ADD, "oppositeDirection" : true, "depth" : 20.15 * mm, "offsetDistance" : 25 * mm});
        }
    });
